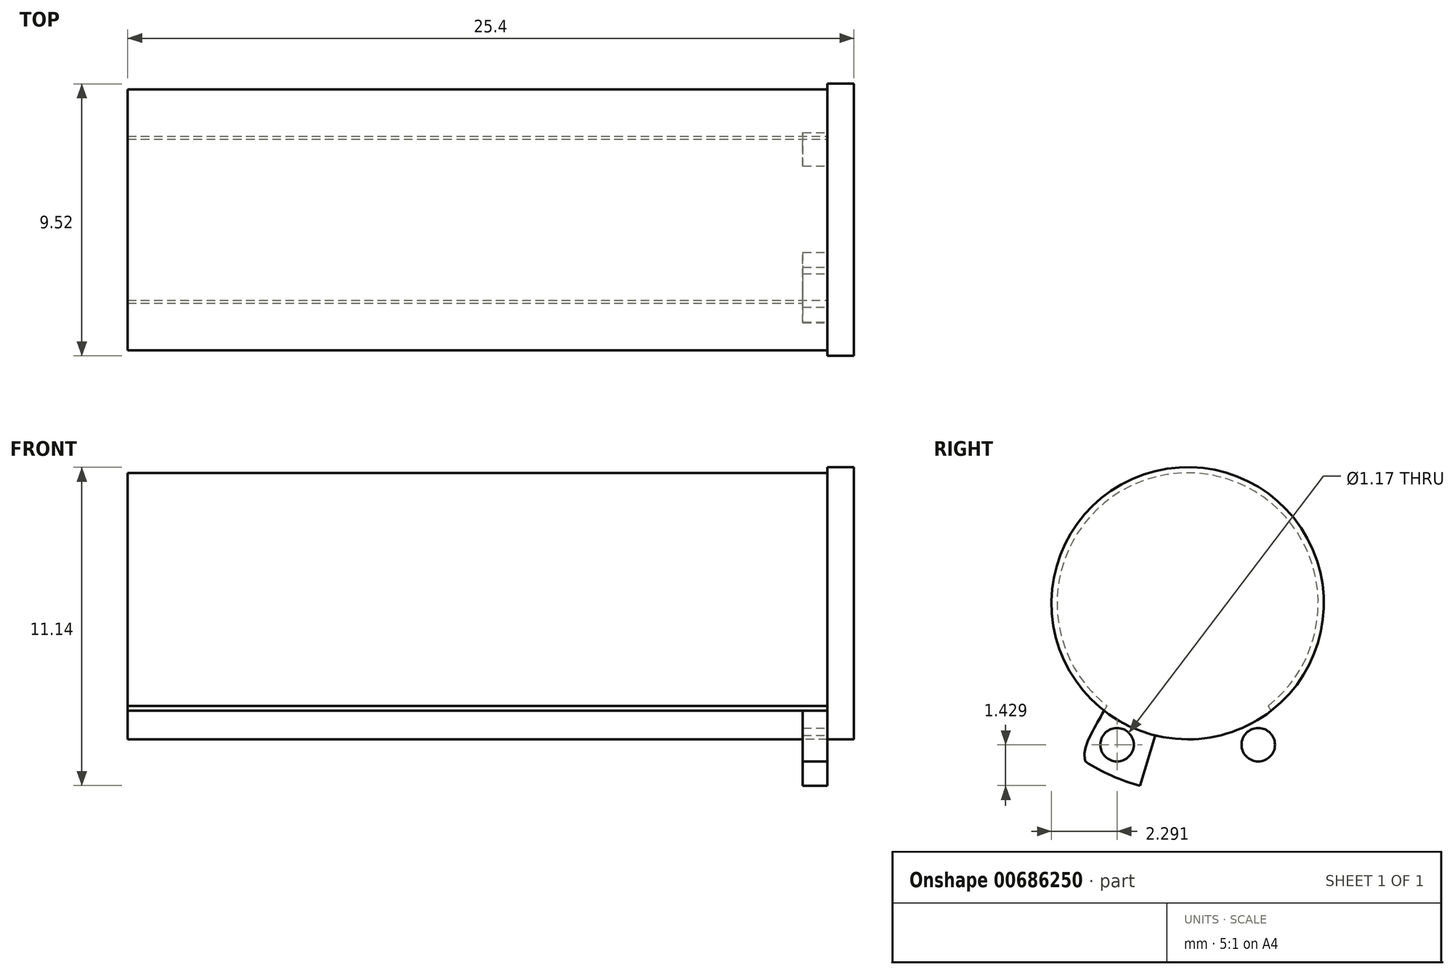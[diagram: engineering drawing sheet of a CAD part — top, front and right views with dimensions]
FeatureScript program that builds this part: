
annotation { "Feature Type Name" : "Feature", "Feature Type Description" : "" }
export const myFeature = defineFeature(function(context is Context, id is Id, definition is map)
    precondition{}
    {
        {
            var Q0;
            Q0=qCreatedBy(makeId("Right.planeOp"),FACE);
            var sketch = newSketch(context, id + "F0", { "sketchPlane" : qUnion([Q0])});
            skCircle(sketch, "E0", {"center": v(0, 0) * mm, "radius": 4.76 * mm});
            skSolve(sketch);
        }
        {
            var Q0;
            Q0=qSketchRegion(id+"F0",true);
            extrude(context, id + "F1", {"entities" : qUnion([Q0]), "depth" : 12.7 * mm, "offsetDistance" : 25.4 * mm});
        }
        {
            var Q0;
            Q0=qCreatedBy(makeId("Top.planeOp"),FACE);
            var sketch = newSketch(context, id + "F2", { "sketchPlane" : qUnion([Q0])});
            skLineSegment(sketch, "E1.bottom", {"start": v(11.77, 6.6) * mm, "end": v(10.91, 6.6) * mm});
            skLineSegment(sketch, "E1.top", {"start": v(11.77, 2.91) * mm, "end": v(10.91, 2.91) * mm});
            skLineSegment(sketch, "E1.left", {"start": v(11.77, 6.6) * mm, "end": v(11.77, 2.91) * mm});
            skLineSegment(sketch, "E1.right", {"start": v(10.91, 6.6) * mm, "end": v(10.91, 2.91) * mm});
            skLineSegment(sketch, "E2", {"start": v(15.49, 0) * mm, "end": v(7.73, 0) * mm, "construction": true});
            skSolve(sketch);
        }
        {
            var Q0;
            Q0=qSketchRegion(id+"F2",true);
            var Q1;
            Q1=sQuery(id+"F2.wireOp",EDGE,"E2");
            revolve(context, id + "F3", {"surfaceOperationType" : NewSurfaceOperationType.NEW, "entities" : qUnion([Q0]), "axis" : qUnion([Q1]), "revolveType" : RevolveType.FULL, "oppositeDirection" : true});
        }
        {
            var Q0;
            Q0=makeQuery(id+"F1.opExtrude","SWEPT_BODY",BODY,{"disambiguationData":[OSD([sQuery(id+"F0.wireOp",EDGE,"E0")])]});
            var Q1;
            Q1=qCreatedBy(makeId("Right.planeOp"),FACE);
            mirror(context, id + "F4", {"operationType" : NewBodyOperationType.ADD, "entities" : qUnion([Q0]), "mirrorPlane" : qUnion([Q1])});
        }
        {
            var Q0;
            Q0=makeQuery(id+"F3.opRevolve","SWEPT_FACE",FACE,{"disambiguationData":[OSD([sQuery(id+"F2.wireOp",EDGE,"E1.left")])]});
            var sketch = newSketch(context, id + "F5", { "sketchPlane" : qUnion([Q0])});
            skLineSegment(sketch, "E3", {"start": v(-0.6, -2.85) * mm, "end": v(-1.67, -6.38) * mm});
            skLineSegment(sketch, "E4.MirrorCS", {"start": v(0.6, -2.85) * mm, "end": v(1.67, -6.38) * mm});
            skFitSpline(sketch, "E5", {"points": [v(-3.58, -5.54) * mm, v(-3.58, -5.1) * mm, v(-2.82, -3.6) * mm], "startDerivative": vector(-0.23, 1.14) * mm, "endDerivative": vector(1.53, 2.58) * mm});
            skFitSpline(sketch, "E6.MirrorCS", {"points": [v(3.58, -5.54) * mm, v(3.58, -5.1) * mm, v(2.82, -3.6) * mm], "startDerivative": vector(0.23, 1.14) * mm, "endDerivative": vector(-1.53, 2.58) * mm});
            skArc(sketch, "E7.trimOffspring", {"start": v(2.82, -3.6) * mm, "mid": v(0, 4.56) * mm, "end": v(-2.82, -3.6) * mm});
            skCircle(sketch, "E8", {"center": v(-2.47, -4.95) * mm, "radius": 0.59 * mm});
            skCircle(sketch, "E9.MirrorC", {"center": v(2.47, -4.95) * mm, "radius": 0.59 * mm});
            skSolve(sketch);
        }
        {
            var Q0;
            {var subQ0=sQuery(id+"F5.wireOp",EDGE,"E3");Q0=makeQuery(id+"F5.imprint","IMPRINT",FACE,{"disambiguationData":[TD([[makeQuery(id+"F5.imprint","IMPRINT",EDGE,{"derivedFrom":subQ0}),1.0]])]});}
            var Q1;
            {var subQ0=sQuery(id+"F5.wireOp",EDGE,"E5");Q1=makeQuery(id+"F5.imprint","IMPRINT",FACE,{"disambiguationData":[TD([[makeQuery(id+"F5.imprint","IMPRINT",EDGE,{"derivedFrom":subQ0}),1.0]])]});}
            var Q2;
            Q2=makeQuery(id+"F5.imprint","IMPRINT",FACE,{"disambiguationData":[TD([[makeQuery(id+"F5.imprint","IMPRINT",EDGE,{"derivedFrom":sQuery(id+"F5.wireOp",EDGE,"E8")}),1.0]])]});
            var Q3;
            Q3=makeQuery(id+"F5.imprint","IMPRINT",FACE,{"disambiguationData":[TD([[makeQuery(id+"F5.imprint","IMPRINT",EDGE,{"derivedFrom":sQuery(id+"F5.wireOp",EDGE,"E9.MirrorC")}),-1.0]])]});
            extrude(context, id + "F6", {"entities" : qUnion([Q0, Q1, Q2, Q3]), "operationType" : NewBodyOperationType.REMOVE, "oppositeDirection" : true, "depth" : 25.4 * mm, "offsetDistance" : 25.4 * mm});
        }
    });
